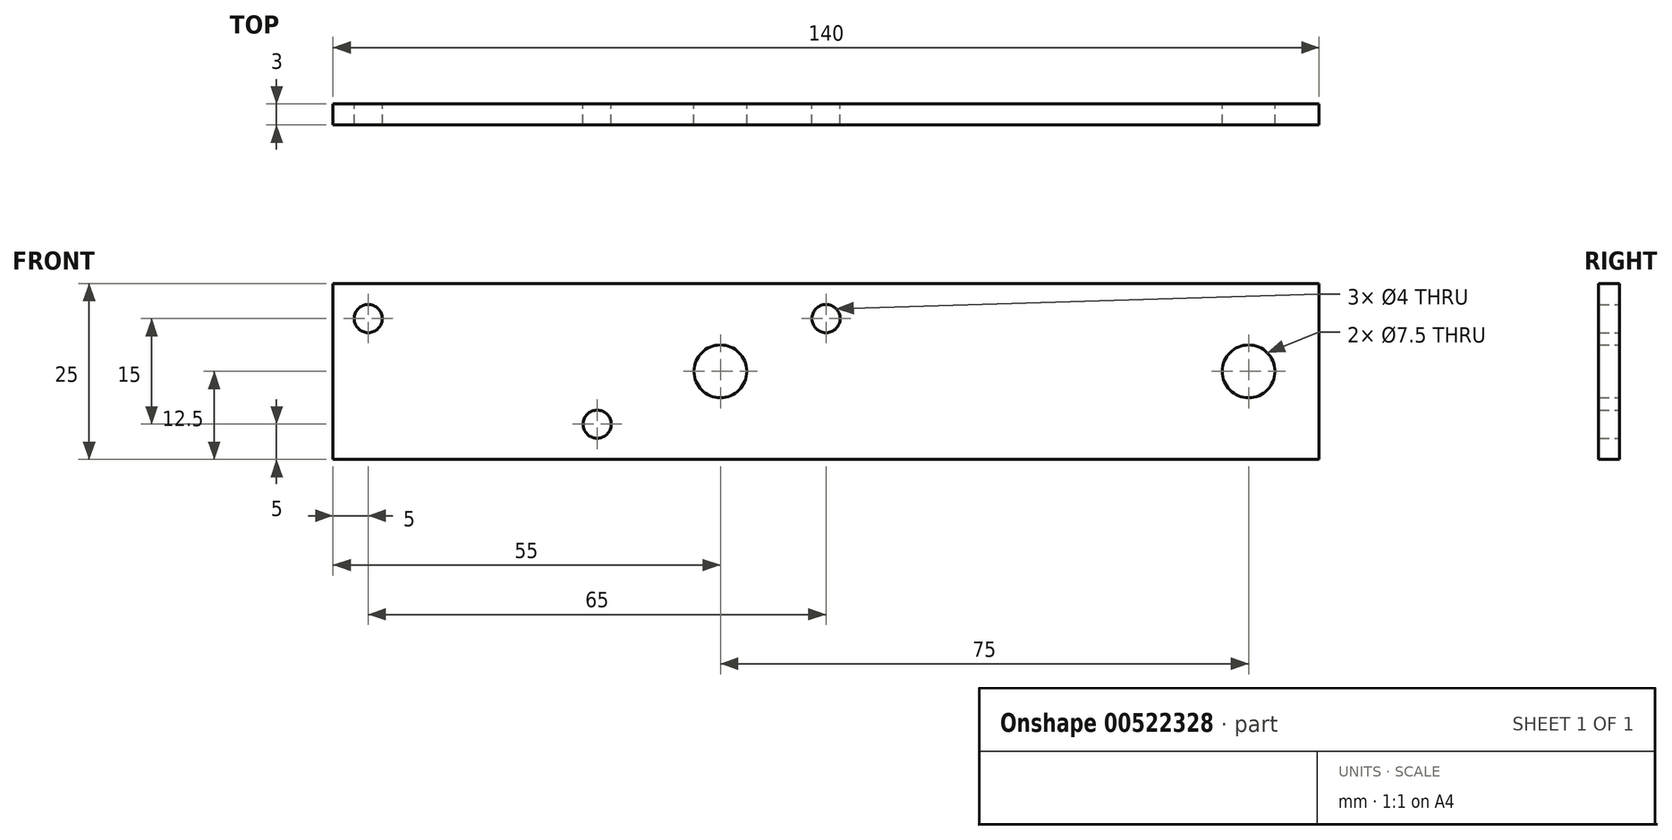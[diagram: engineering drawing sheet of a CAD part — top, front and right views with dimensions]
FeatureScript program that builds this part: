
annotation { "Feature Type Name" : "Feature", "Feature Type Description" : "" }
export const myFeature = defineFeature(function(context is Context, id is Id, definition is map)
    precondition{}
    {
        {
            var Q0;
            Q0=qCreatedBy(makeId("Front.planeOp"),FACE);
            var sketch = newSketch(context, id + "F0", { "sketchPlane" : qUnion([Q0])});
            skLineSegment(sketch, "E0.bottom", {"start": v(70, 12.5) * mm, "end": v(-70, 12.5) * mm});
            skLineSegment(sketch, "E0.top", {"start": v(70, -12.5) * mm, "end": v(-70, -12.5) * mm});
            skLineSegment(sketch, "E0.left", {"start": v(70, 12.5) * mm, "end": v(70, -12.5) * mm});
            skLineSegment(sketch, "E0.right", {"start": v(-70, 12.5) * mm, "end": v(-70, -12.5) * mm});
            skPoint(sketch, "E0.middle", {"position": v(0, 0) * mm});
            skCircle(sketch, "E1", {"center": v(60, 0) * mm, "radius": 3.75 * mm});
            skCircle(sketch, "E2", {"center": v(-15, 0) * mm, "radius": 3.75 * mm});
            skCircle(sketch, "E3", {"center": v(0, 7.5) * mm, "radius": 2 * mm});
            skCircle(sketch, "E4", {"center": v(-65, 7.5) * mm, "radius": 2 * mm});
            skCircle(sketch, "E5", {"center": v(-32.5, -7.5) * mm, "radius": 2 * mm});
            skLineSegment(sketch, "E6", {"start": v(-65, 7.5) * mm, "end": v(0, 7.5) * mm, "construction": true});
            skLineSegment(sketch, "E7", {"start": v(-32.5, -7.5) * mm, "end": v(-32.5, 7.5) * mm, "construction": true});
            skPoint(sketch, "E8", {"position": v(-32.5, 7.5) * mm});
            skSolve(sketch);
        }
        {
            var Q0;
            Q0 = qSketchRegion(id + "F0", true);
            extrude(context, id + "F1", {"entities" : qUnion([Q0]), "depth" : 3 * mm, "offsetDistance" : 25 * mm});
        }
    });
